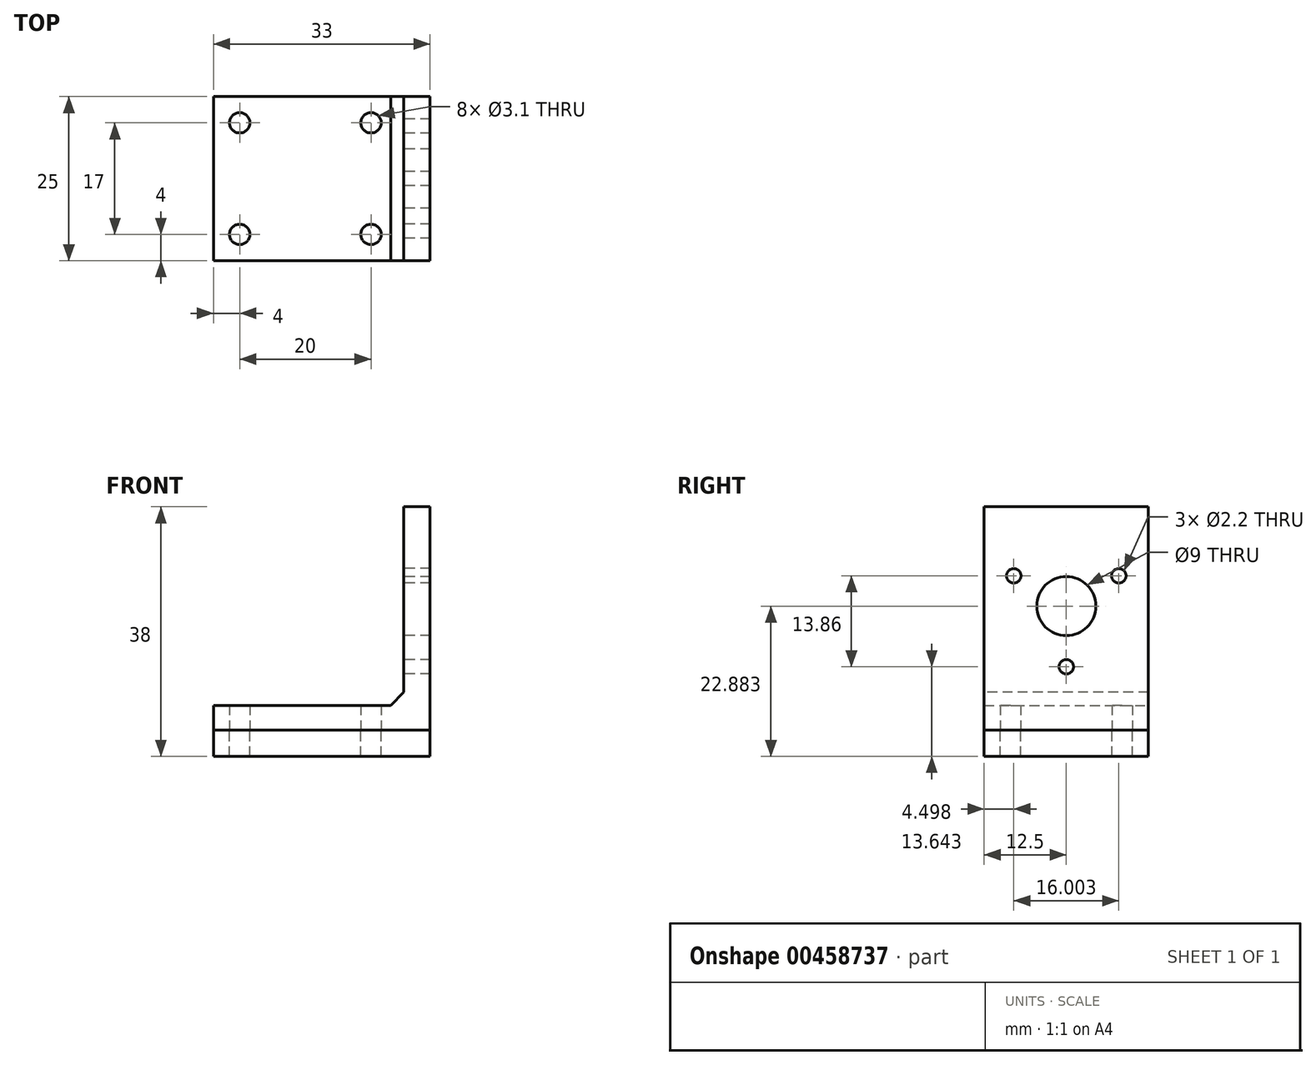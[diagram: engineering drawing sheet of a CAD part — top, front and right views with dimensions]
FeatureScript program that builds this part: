
annotation { "Feature Type Name" : "Feature", "Feature Type Description" : "" }
export const myFeature = defineFeature(function(context is Context, id is Id, definition is map)
    precondition{}
    {
        {
            var Q0;
            Q0=qCreatedBy(makeId("Front.planeOp"),FACE);
            var sketch = newSketch(context, id + "F0", { "sketchPlane" : qUnion([Q0])});
            skLineSegment(sketch, "E0.bottom", {"start": v(0, 0) * mm, "end": v(33, 0) * mm});
            skLineSegment(sketch, "E0.top", {"start": v(0, 3.77) * mm, "end": v(33, 3.77) * mm});
            skLineSegment(sketch, "E0.left", {"start": v(0, 0) * mm, "end": v(0, 3.77) * mm});
            skLineSegment(sketch, "E0.right", {"start": v(33, 0) * mm, "end": v(33, 3.77) * mm});
            skLineSegment(sketch, "E1.bottom", {"start": v(33, 0) * mm, "end": v(29, 0) * mm});
            skLineSegment(sketch, "E1.top", {"start": v(33, 34) * mm, "end": v(29, 34) * mm});
            skLineSegment(sketch, "E1.left", {"start": v(33, 0) * mm, "end": v(33, 34) * mm});
            skLineSegment(sketch, "E1.right", {"start": v(29, 0) * mm, "end": v(29, 34) * mm});
            skSolve(sketch);
        }
        {
            var Q0;
            Q0 = qSketchRegion(id + "F0", true);
            extrude(context, id + "F1", {"entities" : qUnion([Q0]), "depth" : 25 * mm, "offsetDistance" : 25 * mm});
        }
        {
            var Q0;
            Q0=makeQuery(id+"F1.opExtrude","SWEPT_FACE",FACE,{"disambiguationData":[OSD([sQuery(id+"F0.wireOp",EDGE,"E1.right")])]});
            var sketch = newSketch(context, id + "F2", { "sketchPlane" : qUnion([Q0])});
            skCircle(sketch, "E2.0", {"center": v(12.5, 18.88) * mm, "radius": 11.25 * mm});
            skCircle(sketch, "E3.0", {"center": v(4.5, 23.5) * mm, "radius": 1.1 * mm});
            skCircle(sketch, "E4.0", {"center": v(12.5, 18.88) * mm, "radius": 4.5 * mm});
            skCircle(sketch, "E5.0", {"center": v(12.5, 9.64) * mm, "radius": 1.1 * mm});
            skCircle(sketch, "E6.0", {"center": v(20.5, 23.5) * mm, "radius": 1.1 * mm});
            skSolve(sketch);
        }
        {
            var Q0;
            Q0=makeQuery(id+"F2.imprint","IMPRINT",FACE,{"disambiguationData":[TD([[makeQuery(id+"F2.imprint","IMPRINT",EDGE,{"derivedFrom":sQuery(id+"F2.wireOp",EDGE,"E3.0")}),1.0]])]});
            var Q1;
            Q1=makeQuery(id+"F2.imprint","IMPRINT",FACE,{"disambiguationData":[TD([[makeQuery(id+"F2.imprint","IMPRINT",EDGE,{"derivedFrom":sQuery(id+"F2.wireOp",EDGE,"E6.0")}),1.0]])]});
            var Q2;
            Q2=makeQuery(id+"F2.imprint","IMPRINT",FACE,{"disambiguationData":[TD([[makeQuery(id+"F2.imprint","IMPRINT",EDGE,{"derivedFrom":sQuery(id+"F2.wireOp",EDGE,"E5.0")}),1.0]])]});
            var Q3;
            Q3=makeQuery(id+"F2.imprint","IMPRINT",FACE,{"disambiguationData":[TD([[makeQuery(id+"F2.imprint","IMPRINT",EDGE,{"derivedFrom":sQuery(id+"F2.wireOp",EDGE,"E4.0")}),1.0]])]});
            extrude(context, id + "F3", {"entities" : qUnion([Q0, Q1, Q2, Q3]), "operationType" : NewBodyOperationType.REMOVE, "oppositeDirection" : true, "depth" : 25 * mm, "offsetDistance" : 25 * mm});
        }
        {
            var Q0;
            Q0=makeQuery(id+"F1.opExtrude","SWEPT_FACE",FACE,{"disambiguationData":[OSD([sQuery(id+"F0.wireOp",EDGE,"E0.bottom"),sQuery(id+"F0.wireOp",EDGE,"E1.bottom")])]});
            var sketch = newSketch(context, id + "F4", { "sketchPlane" : qUnion([Q0])});
            skLineSegment(sketch, "E7.bottom", {"start": v(33, 25) * mm, "end": v(28, 25) * mm});
            skLineSegment(sketch, "E7.top", {"start": v(33, 0) * mm, "end": v(28, 0) * mm});
            skLineSegment(sketch, "E7.left", {"start": v(33, 25) * mm, "end": v(33, 0) * mm});
            skLineSegment(sketch, "E7.right", {"start": v(28, 25) * mm, "end": v(28, 0) * mm});
            skLineSegment(sketch, "E8.bottom", {"start": v(28, 0) * mm, "end": v(0, 0) * mm});
            skLineSegment(sketch, "E8.top", {"start": v(28, 25) * mm, "end": v(0, 25) * mm});
            skLineSegment(sketch, "E8.left", {"start": v(28, 0) * mm, "end": v(28, 25) * mm});
            skLineSegment(sketch, "E8.right", {"start": v(0, 0) * mm, "end": v(0, 25) * mm});
            skLineSegment(sketch, "E9.0", {"start": v(4, 4) * mm, "end": v(4, 21) * mm});
            skLineSegment(sketch, "E9.1", {"start": v(24, 4) * mm, "end": v(4, 4) * mm});
            skLineSegment(sketch, "E9.2", {"start": v(24, 4) * mm, "end": v(24, 21) * mm});
            skLineSegment(sketch, "E9.3", {"start": v(24, 21) * mm, "end": v(4, 21) * mm});
            skCircle(sketch, "E10", {"center": v(4, 21) * mm, "radius": 1.55 * mm});
            skCircle(sketch, "E11", {"center": v(4, 4) * mm, "radius": 1.55 * mm});
            skCircle(sketch, "E12", {"center": v(24, 21) * mm, "radius": 1.55 * mm});
            skCircle(sketch, "E13", {"center": v(24, 4) * mm, "radius": 1.55 * mm});
            skSolve(sketch);
        }
        {
            var Q0;
            {var subQ0=sQuery(id+"F4.wireOp",EDGE,"E9.3");var subQ1=sQuery(id+"F4.wireOp",EDGE,"E9.0");var subQ2=makeQuery(id+"F4.imprint","INTERSECT",VERTEX,{"derivedFrom":[subQ1,subQ0]});Q0=makeQuery(id+"F4.imprint","IMPRINT",FACE,{"disambiguationData":[TD([[makeQuery(id+"F4.imprint","IMPRINT",EDGE,{"disambiguationData":[TD([[subQ2,1.0]])],"derivedFrom":subQ1}),1.0]])]});}
            var Q1;
            {var subQ0=sQuery(id+"F4.wireOp",EDGE,"E9.3");var subQ1=sQuery(id+"F4.wireOp",EDGE,"E9.0");var subQ2=makeQuery(id+"F4.imprint","INTERSECT",VERTEX,{"derivedFrom":[subQ1,subQ0]});Q1=makeQuery(id+"F4.imprint","IMPRINT",FACE,{"disambiguationData":[TD([[makeQuery(id+"F4.imprint","IMPRINT",EDGE,{"disambiguationData":[TD([[subQ2,1.0]])],"derivedFrom":subQ1}),-1.0]])]});}
            var Q2;
            {var subQ0=sQuery(id+"F4.wireOp",EDGE,"E9.3");var subQ1=sQuery(id+"F4.wireOp",EDGE,"E9.2");var subQ2=makeQuery(id+"F4.imprint","INTERSECT",VERTEX,{"derivedFrom":[subQ1,subQ0]});Q2=makeQuery(id+"F4.imprint","IMPRINT",FACE,{"disambiguationData":[TD([[makeQuery(id+"F4.imprint","IMPRINT",EDGE,{"disambiguationData":[TD([[subQ2,1.0]])],"derivedFrom":subQ1}),-1.0]])]});}
            var Q3;
            {var subQ0=sQuery(id+"F4.wireOp",EDGE,"E9.3");var subQ1=sQuery(id+"F4.wireOp",EDGE,"E9.2");var subQ2=makeQuery(id+"F4.imprint","INTERSECT",VERTEX,{"derivedFrom":[subQ1,subQ0]});Q3=makeQuery(id+"F4.imprint","IMPRINT",FACE,{"disambiguationData":[TD([[makeQuery(id+"F4.imprint","IMPRINT",EDGE,{"disambiguationData":[TD([[subQ2,1.0]])],"derivedFrom":subQ1}),1.0]])]});}
            var Q4;
            {var subQ0=sQuery(id+"F4.wireOp",EDGE,"E9.2");var subQ1=sQuery(id+"F4.wireOp",EDGE,"E9.1");var subQ2=makeQuery(id+"F4.imprint","INTERSECT",VERTEX,{"derivedFrom":[subQ1,subQ0]});Q4=makeQuery(id+"F4.imprint","IMPRINT",FACE,{"disambiguationData":[TD([[makeQuery(id+"F4.imprint","IMPRINT",EDGE,{"disambiguationData":[TD([[subQ2,-1.0]])],"derivedFrom":subQ1}),1.0]])]});}
            var Q5;
            {var subQ0=sQuery(id+"F4.wireOp",EDGE,"E9.2");var subQ1=sQuery(id+"F4.wireOp",EDGE,"E9.1");var subQ2=makeQuery(id+"F4.imprint","INTERSECT",VERTEX,{"derivedFrom":[subQ1,subQ0]});Q5=makeQuery(id+"F4.imprint","IMPRINT",FACE,{"disambiguationData":[TD([[makeQuery(id+"F4.imprint","IMPRINT",EDGE,{"disambiguationData":[TD([[subQ2,-1.0]])],"derivedFrom":subQ1}),-1.0]])]});}
            var Q6;
            {var subQ0=sQuery(id+"F4.wireOp",EDGE,"E9.1");var subQ1=sQuery(id+"F4.wireOp",EDGE,"E9.0");var subQ2=makeQuery(id+"F4.imprint","INTERSECT",VERTEX,{"derivedFrom":[subQ1,subQ0]});Q6=makeQuery(id+"F4.imprint","IMPRINT",FACE,{"disambiguationData":[TD([[makeQuery(id+"F4.imprint","IMPRINT",EDGE,{"disambiguationData":[TD([[subQ2,-1.0]])],"derivedFrom":subQ1}),-1.0]])]});}
            var Q7;
            {var subQ0=sQuery(id+"F4.wireOp",EDGE,"E9.1");var subQ1=sQuery(id+"F4.wireOp",EDGE,"E9.0");var subQ2=makeQuery(id+"F4.imprint","INTERSECT",VERTEX,{"derivedFrom":[subQ1,subQ0]});Q7=makeQuery(id+"F4.imprint","IMPRINT",FACE,{"disambiguationData":[TD([[makeQuery(id+"F4.imprint","IMPRINT",EDGE,{"disambiguationData":[TD([[subQ2,-1.0]])],"derivedFrom":subQ1}),1.0]])]});}
            extrude(context, id + "F5", {"entities" : qUnion([Q0, Q1, Q2, Q3, Q4, Q5, Q6, Q7]), "operationType" : NewBodyOperationType.REMOVE, "oppositeDirection" : true, "depth" : 25 * mm, "offsetDistance" : 25 * mm});
        }
        {
            var Q0;
            Q0=makeQuery(id+"F1.opExtrude","SWEPT_FACE",FACE,{"disambiguationData":[OSD([sQuery(id+"F0.wireOp",EDGE,"E0.bottom"),sQuery(id+"F0.wireOp",EDGE,"E1.bottom")])]});
            extrude(context, id + "F6", {"entities" : qUnion([Q0]), "depth" : 4 * mm, "offsetDistance" : 25 * mm});
        }
        {
            var Q0;
            Q0=makeQuery(id+"F1.opExtrude","SWEPT_EDGE",EDGE,{"disambiguationData":[OSD([sQuery(id+"F0.wireOp",EDGE,"E0.top"),sQuery(id+"F0.wireOp",EDGE,"E1.right")])]});
            chamfer(context, id + "F7", {"entities" : qUnion([Q0]), "width" : 2 * mm, "tangentPropagation" : true});
        }
    });
